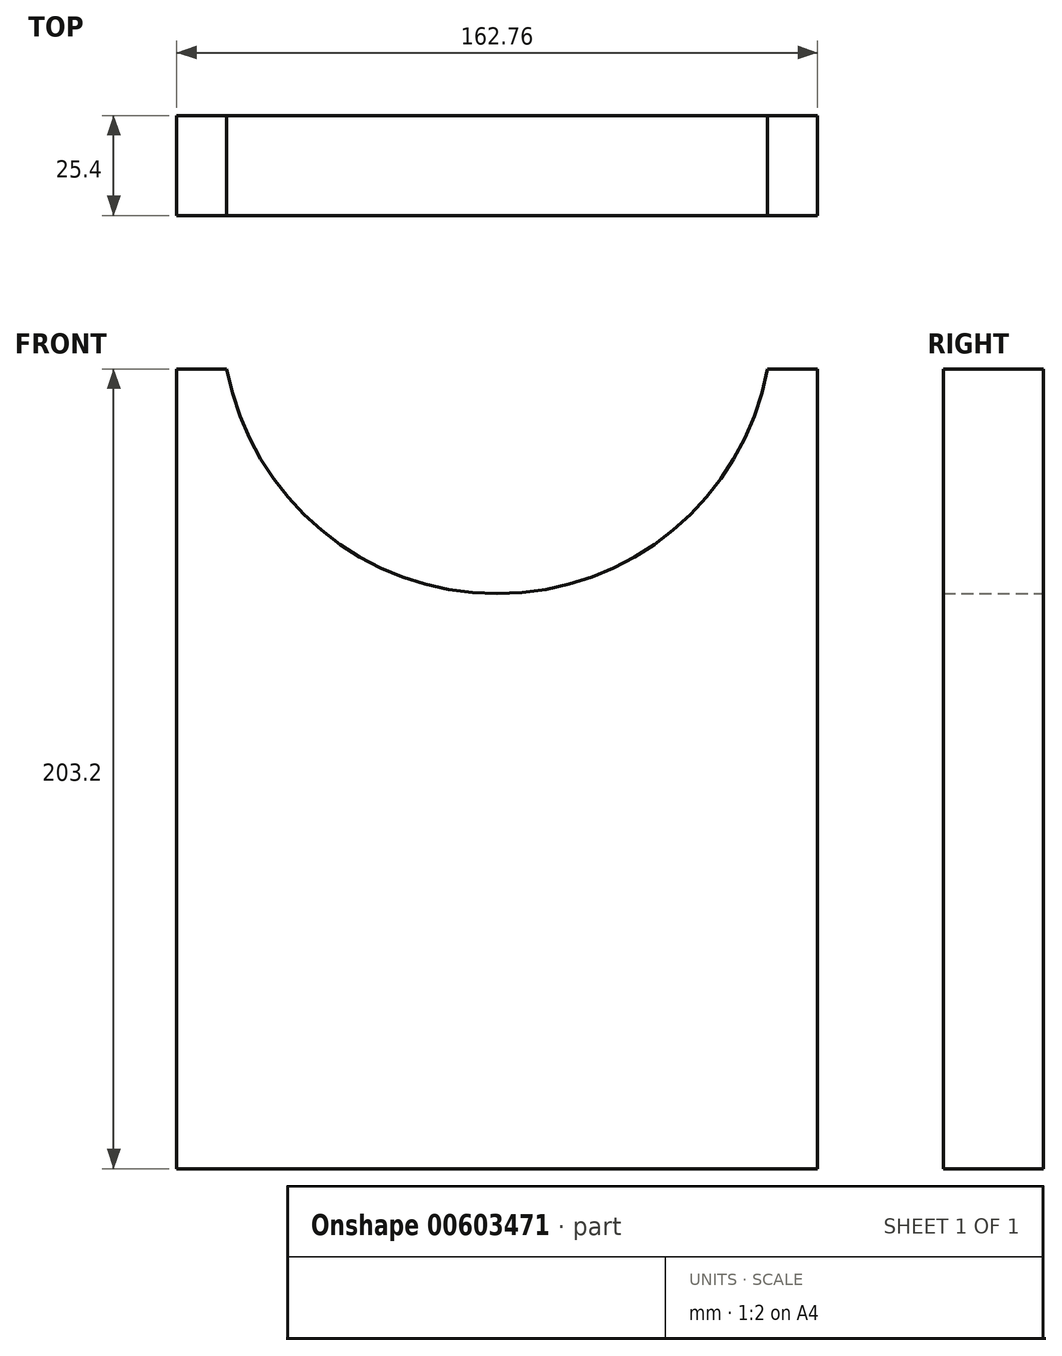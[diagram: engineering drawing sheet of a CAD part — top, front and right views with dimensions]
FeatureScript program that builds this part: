
annotation { "Feature Type Name" : "Feature", "Feature Type Description" : "" }
export const myFeature = defineFeature(function(context is Context, id is Id, definition is map)
    precondition{}
    {
        {
            var Q0;
            Q0=qCreatedBy(makeId("Front.planeOp"),FACE);
            var sketch = newSketch(context, id + "F0", { "sketchPlane" : qUnion([Q0])});
            skLineSegment(sketch, "E0.bottom", {"start": v(0, 0) * mm, "end": v(162.76, 0) * mm});
            skLineSegment(sketch, "E0.top", {"start": v(0, 203.2) * mm, "end": v(12.7, 203.2) * mm});
            skLineSegment(sketch, "E0.left", {"start": v(0, 0) * mm, "end": v(0, 203.2) * mm});
            skLineSegment(sketch, "E0.right", {"start": v(162.76, 0) * mm, "end": v(162.76, 203.2) * mm});
            skLineSegment(sketch, "E1", {"start": v(12.7, 228.64) * mm, "end": v(12.7, 203.2) * mm, "construction": true});
            skLineSegment(sketch, "E2", {"start": v(150.06, 228.64) * mm, "end": v(150.06, 203.2) * mm, "construction": true});
            skArc(sketch, "E3", {"start": v(12.7, 203.2) * mm, "mid": v(81.38, 146.07) * mm, "end": v(150.06, 203.2) * mm});
            skArc(sketch, "E4", {"start": v(150.06, 203.2) * mm, "mid": v(81.38, 285.77) * mm, "end": v(12.7, 203.2) * mm, "construction": true});
            skLineSegment(sketch, "E5.trimOffspring", {"start": v(150.06, 203.2) * mm, "end": v(162.76, 203.2) * mm});
            skSolve(sketch);
        }
        {
            var Q0;
            Q0=makeQuery(id+"F0.imprint","IMPRINT",FACE,{"disambiguationData":[TD([[makeQuery(id+"F0.imprint","IMPRINT",EDGE,{"derivedFrom":sQuery(id+"F0.wireOp",EDGE,"E0.bottom")}),1.0]])]});
            extrude(context, id + "F1", {"entities" : qUnion([Q0]), "depth" : 25.4 * mm, "offsetDistance" : 25.4 * mm});
        }
    });
